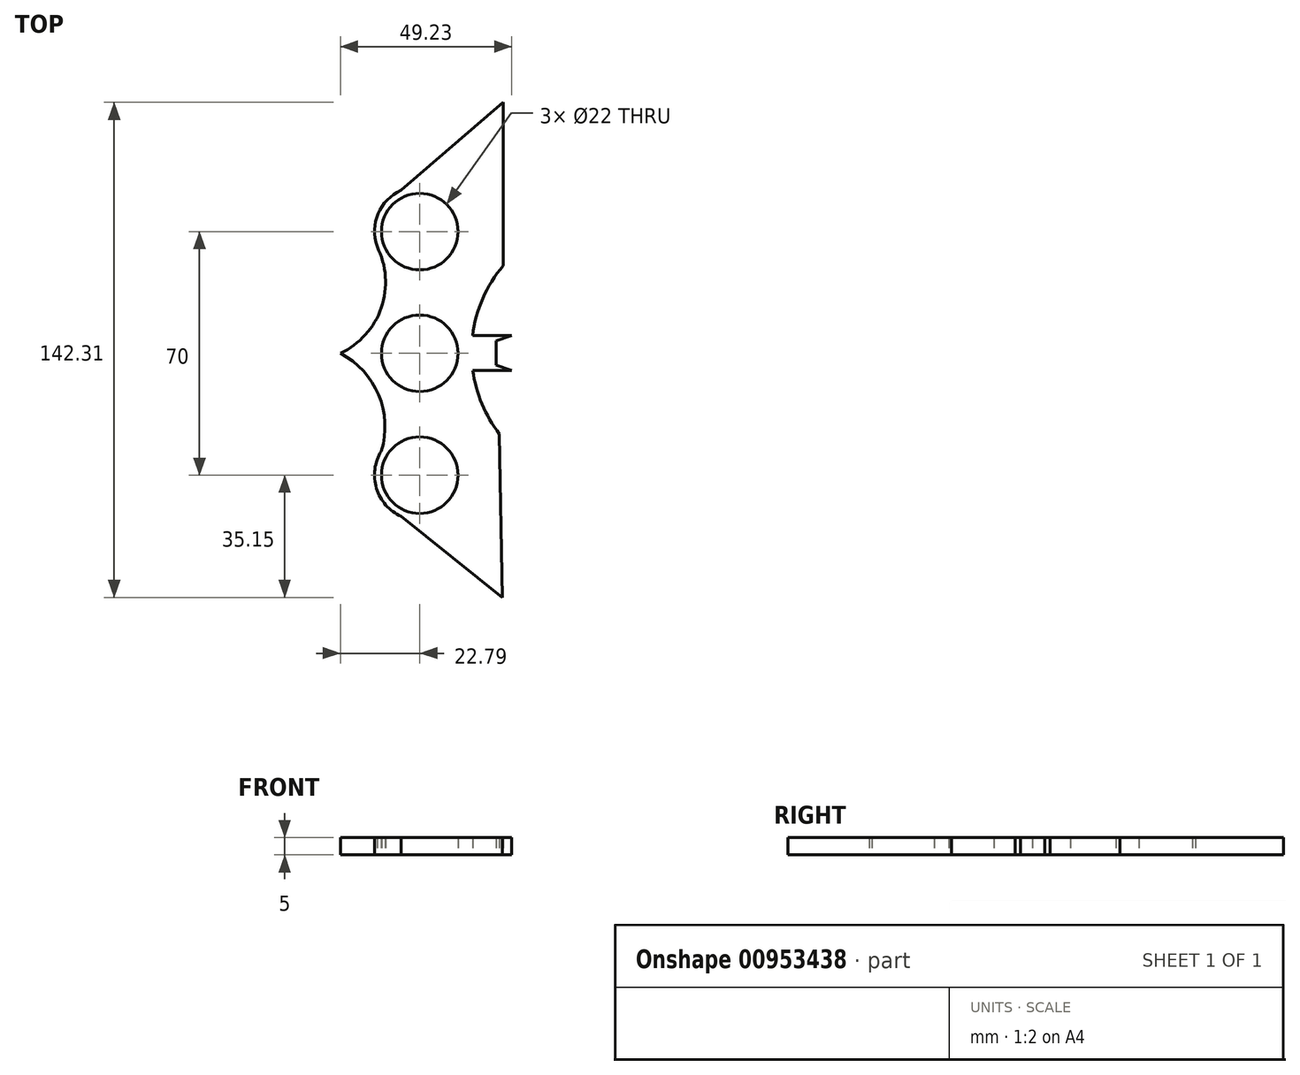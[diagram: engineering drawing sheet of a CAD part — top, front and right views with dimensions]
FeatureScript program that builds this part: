
annotation { "Feature Type Name" : "Feature", "Feature Type Description" : "" }
export const myFeature = defineFeature(function(context is Context, id is Id, definition is map)
    precondition{}
    {
        {
            var Q0;
            Q0=qCreatedBy(makeId("Top.planeOp"),FACE);
            var sketch = newSketch(context, id + "F0", { "sketchPlane" : qUnion([Q0])});
            skCircle(sketch, "E0", {"center": v(0, 0) * mm, "radius": 11 * mm});
            skCircle(sketch, "E1", {"center": v(0, 35) * mm, "radius": 13 * mm});
            skCircle(sketch, "E2.1.0", {"center": v(0, -35) * mm, "radius": 13 * mm});
            skArc(sketch, "E3", {"start": v(-22.8, 0) * mm, "mid": v(-11.03, 13.13) * mm, "end": v(-12.27, 30.72) * mm});
            skArc(sketch, "E4", {"start": v(-11.03, -28.12) * mm, "mid": v(-11.82, -11.93) * mm, "end": v(-22.8, 0) * mm});
            skPoint(sketch, "E4.startSnap0", {"position": v(-11.03, 13.13) * mm});
            skCircle(sketch, "E5", {"center": v(0, 35) * mm, "radius": 11 * mm});
            skCircle(sketch, "E6.1.0", {"center": v(0, -35) * mm, "radius": 11 * mm});
            skLineSegment(sketch, "E7", {"start": v(23.93, 72.16) * mm, "end": v(23.98, 25.16) * mm});
            skLineSegment(sketch, "E8.trimOffspring", {"start": v(22.9, -23.15) * mm, "end": v(23.76, -70.15) * mm});
            skArc(sketch, "E9", {"start": v(23.98, 25.16) * mm, "mid": v(18.11, 15.76) * mm, "end": v(15.17, 5.08) * mm});
            skLineSegment(sketch, "E10", {"start": v(15.17, 5.08) * mm, "end": v(26.44, 5.08) * mm});
            skLineSegment(sketch, "E11", {"start": v(26.44, 5.08) * mm, "end": v(22, 3.58) * mm});
            skLineSegment(sketch, "E12", {"start": v(22, 3.58) * mm, "end": v(22, -3.39) * mm});
            skLineSegment(sketch, "E13", {"start": v(22, -3.39) * mm, "end": v(26.44, -4.89) * mm});
            skLineSegment(sketch, "E14", {"start": v(26.44, -4.89) * mm, "end": v(15.24, -4.89) * mm});
            skLineSegment(sketch, "E15", {"start": v(23.93, 72.16) * mm, "end": v(-5.33, 46.86) * mm});
            skLineSegment(sketch, "E16", {"start": v(-5.33, -46.86) * mm, "end": v(23.76, -70.15) * mm});
            skArc(sketch, "E17.trimOffspring", {"start": v(15.24, -4.89) * mm, "mid": v(17.87, -14.52) * mm, "end": v(22.9, -23.15) * mm});
            skSolve(sketch);
        }
        {
            var Q0;
            Q0=makeQuery(id+"F0.imprint","IMPRINT",FACE,{"disambiguationData":[TD([[makeQuery(id+"F0.imprint","IMPRINT",EDGE,{"derivedFrom":sQuery(id+"F0.wireOp",EDGE,"E0")}),-1.0]])]});
            var Q1;
            Q1=makeQuery(id+"F0.imprint","IMPRINT",FACE,{"disambiguationData":[TD([[makeQuery(id+"F0.imprint","IMPRINT",EDGE,{"derivedFrom":sQuery(id+"F0.wireOp",EDGE,"E5")}),-1.0]])]});
            var Q2;
            Q2=makeQuery(id+"F0.imprint","IMPRINT",FACE,{"disambiguationData":[TD([[makeQuery(id+"F0.imprint","IMPRINT",EDGE,{"derivedFrom":sQuery(id+"F0.wireOp",EDGE,"E6.1.0")}),-1.0]])]});
            extrude(context, id + "F1", {"entities" : qUnion([Q0, Q1, Q2]), "depth" : 5 * mm, "offsetDistance" : 25 * mm});
        }
    });
